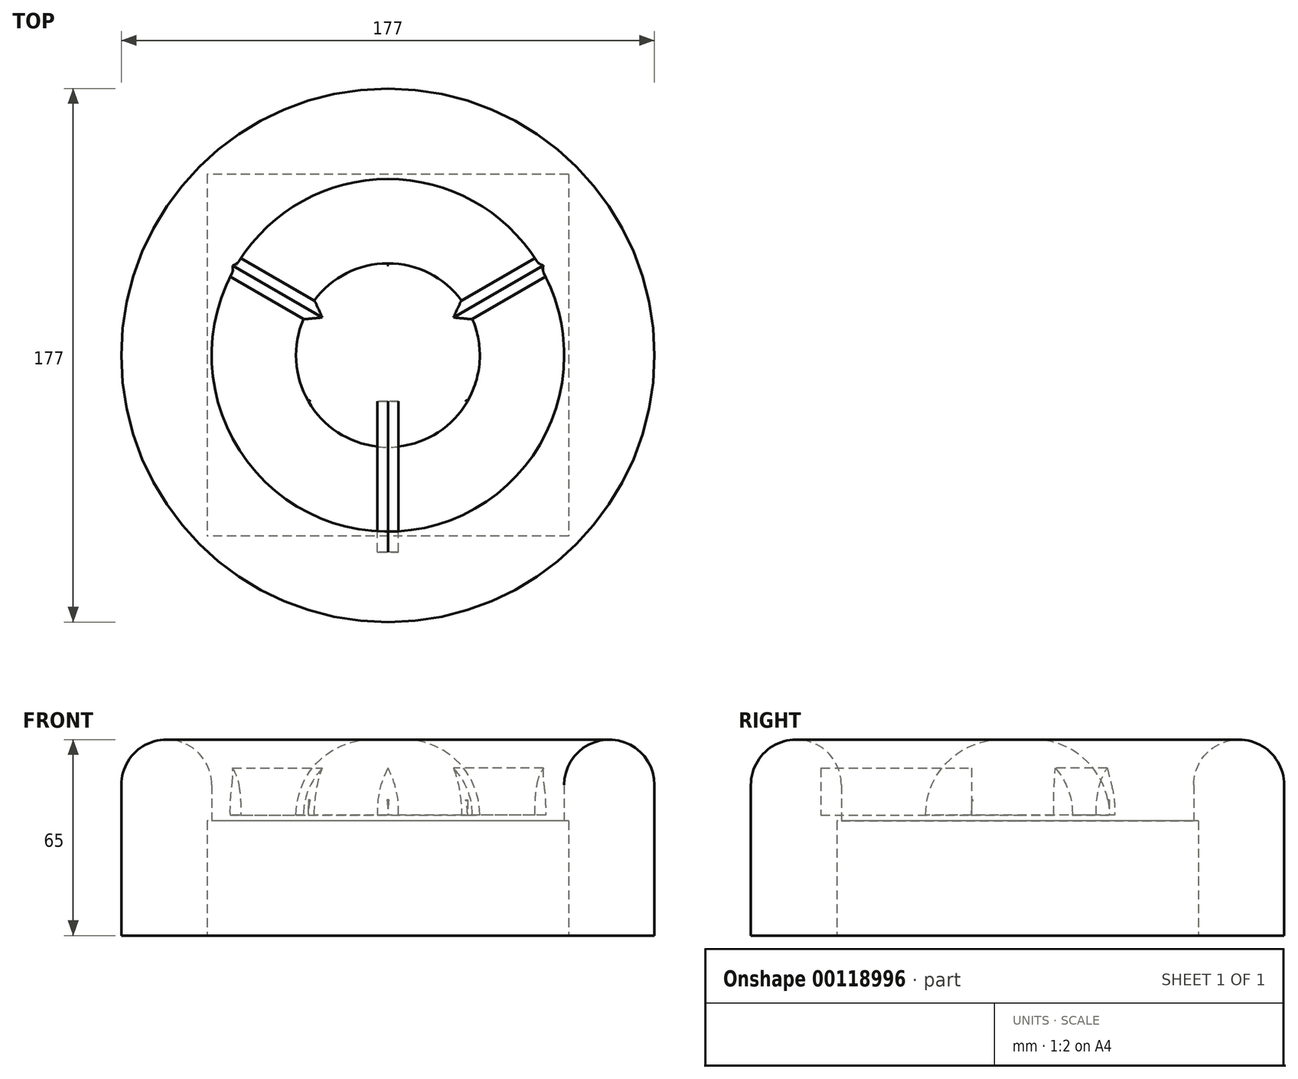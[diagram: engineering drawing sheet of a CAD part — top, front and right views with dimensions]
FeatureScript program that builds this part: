
annotation { "Feature Type Name" : "Feature", "Feature Type Description" : "" }
export const myFeature = defineFeature(function(context is Context, id is Id, definition is map)
    precondition{}
    {
        {
            var Q0;
            Q0=qCreatedBy(makeId("Top.planeOp"),FACE);
            var sketch = newSketch(context, id + "F0", { "sketchPlane" : qUnion([Q0])});
            skCircle(sketch, "E0", {"center": v(0, 0) * mm, "radius": 30.5 * mm});
            skCircle(sketch, "E1", {"center": v(0, 0) * mm, "radius": 58.5 * mm});
            skCircle(sketch, "E2", {"center": v(0, 0) * mm, "radius": 88.5 * mm});
            skLineSegment(sketch, "E3", {"start": v(0, 30.5) * mm, "end": v(-26.41, -15.25) * mm});
            skLineSegment(sketch, "E4", {"start": v(0, 30.5) * mm, "end": v(26.41, -15.25) * mm});
            skLineSegment(sketch, "E5", {"start": v(-26.41, -15.25) * mm, "end": v(26.41, -15.25) * mm});
            skSolve(sketch);
        }
        {
            var Q0;
            Q0=makeQuery(id+"F0.imprint","IMPRINT",FACE,{"disambiguationData":[TD([[makeQuery(id+"F0.imprint","IMPRINT",EDGE,{"derivedFrom":sQuery(id+"F0.wireOp",EDGE,"E0")}),1.0]])]});
            var Q1;
            Q1=makeQuery(id+"F0.imprint","IMPRINT",FACE,{"disambiguationData":[TD([[makeQuery(id+"F0.imprint","IMPRINT",EDGE,{"derivedFrom":sQuery(id+"F0.wireOp",EDGE,"E3")}),1.0]])]});
            extrude(context, id + "F1", {"entities" : qUnion([Q0, Q1]), "depth" : 25 * mm});
        }
        {
            var Q0;
            Q0=makeQuery(id+"F0.imprint","IMPRINT",FACE,{"disambiguationData":[TD([[makeQuery(id+"F0.imprint","IMPRINT",EDGE,{"derivedFrom":sQuery(id+"F0.wireOp",EDGE,"E3")}),1.0]])]});
            extrude(context, id + "F2", {"entities" : qUnion([Q0]), "depth" : 5 * mm});
        }
        {
            var Q0;
            Q0=makeQuery(id+"F1.opExtrude","CAP_EDGE",EDGE,{"disambiguationData":[OSD([sQuery(id+"F0.wireOp",EDGE,"E0")])],"isStart":false});
            fillet(context, id + "F3", {"entities" : qUnion([Q0]), "radius" : 25 * mm, "tangentPropagation" : true, "allowEdgeOverflow" : false});
        }
        {
            var Q0;
            Q0 = qSketchRegion(id + "F0", true);
            extrude(context, id + "F4", {"entities" : qUnion([Q0]), "depth" : 25 * mm, "hasSecondDirection" : true, "secondDirectionOppositeDirection" : true, "secondDirectionDepth" : 40 * mm});
        }
        {
            var Q0;
            Q0=makeQuery(id+"F4.opExtrude","CAP_FACE",FACE,{"disambiguationData":[OSD([sQuery(id+"F0.wireOp",EDGE,"E1"),sQuery(id+"F0.wireOp",EDGE,"E2")])],"isStart":false});
            var Q1;
            Q1=makeQuery(id+"F4.opExtrude","CAP_EDGE",EDGE,{"disambiguationData":[OSD([sQuery(id+"F0.wireOp",EDGE,"E2")])],"isStart":false});
            var Q2;
            Q2=makeQuery(id+"F4.opExtrude","CAP_EDGE",EDGE,{"disambiguationData":[OSD([sQuery(id+"F0.wireOp",EDGE,"E1")])],"isStart":false});
            fillet(context, id + "F5", {"entities" : qUnion([Q0, Q1, Q2]), "radius" : 15 * mm, "tangentPropagation" : true, "allowEdgeOverflow" : false});
        }
        {
            var Q0;
            Q0=makeQuery(id+"F4.opExtrude","CAP_FACE",FACE,{"disambiguationData":[OSD([sQuery(id+"F0.wireOp",EDGE,"E1"),sQuery(id+"F0.wireOp",EDGE,"E2")])],"isStart":true});
            var sketch = newSketch(context, id + "F6", { "sketchPlane" : qUnion([Q0])});
            skLineSegment(sketch, "E6.bottom", {"start": v(60, -60) * mm, "end": v(-60, -60) * mm});
            skLineSegment(sketch, "E6.top", {"start": v(60, 60) * mm, "end": v(-60, 60) * mm});
            skLineSegment(sketch, "E6.left", {"start": v(60, -60) * mm, "end": v(60, 60) * mm});
            skLineSegment(sketch, "E6.right", {"start": v(-60, -60) * mm, "end": v(-60, 60) * mm});
            skPoint(sketch, "E6.middle", {"position": v(0, 0) * mm});
            skSolve(sketch);
        }
        {
            var Q0;
            Q0=makeQuery(id+"F6.imprint","IMPRINT",FACE,{"disambiguationData":[TD([[makeQuery(id+"F6.imprint","IMPRINT",EDGE,{"derivedFrom":sQuery(id+"F6.wireOp",EDGE,"E6.bottom")}),-1.0]])]});
            extrude(context, id + "F7", {"entities" : qUnion([Q0]), "operationType" : NewBodyOperationType.REMOVE, "oppositeDirection" : true, "depth" : 38 * mm});
        }
        {
            var Q0;
            Q0=makeQuery(id+"F2.opExtrude","SWEPT_FACE",FACE,{"disambiguationData":[OSD([sQuery(id+"F0.wireOp",EDGE,"E5")])]});
            var sketch = newSketch(context, id + "F8", { "sketchPlane" : qUnion([Q0])});
            skArc(sketch, "E7", {"start": v(3.5, 0) * mm, "mid": v(2.8, 8) * mm, "end": v(0, 15.53) * mm});
            skArc(sketch, "E8", {"start": v(0, 15.53) * mm, "mid": v(-2.8, 8) * mm, "end": v(-3.5, 0) * mm});
            skLineSegment(sketch, "E9", {"start": v(-3.5, 0) * mm, "end": v(3.5, 0) * mm});
            skSolve(sketch);
        }
        {
            var Q0;
            Q0 = qSketchRegion(id + "F8", true);
            extrude(context, id + "F9", {"entities" : qUnion([Q0]), "depth" : 50 * mm});
        }
        {
            var Q0;
            Q0=makeQuery(id+"F2.opExtrude","SWEPT_FACE",FACE,{"disambiguationData":[OSD([sQuery(id+"F0.wireOp",EDGE,"E3")])]});
            var sketch = newSketch(context, id + "F10", { "sketchPlane" : qUnion([Q0])});
            skArc(sketch, "E10", {"start": v(3.5, 0) * mm, "mid": v(2.8, 8) * mm, "end": v(0, 15.53) * mm});
            skArc(sketch, "E11", {"start": v(0, 15.53) * mm, "mid": v(-2.8, 8) * mm, "end": v(-3.5, 0) * mm});
            skLineSegment(sketch, "E12", {"start": v(-3.5, 0) * mm, "end": v(3.5, 0) * mm});
            skSolve(sketch);
        }
        {
            var Q0;
            {var subQ0=sQuery(id+"F10.wireOp",EDGE,"E11");var subQ1=sQuery(id+"F10.wireOp",EDGE,"E10");var subQ2=makeQuery(id+"F10.imprint","INTERSECT",VERTEX,{"derivedFrom":[subQ1,subQ0]});Q0=makeQuery(id+"F10.imprint","IMPRINT",FACE,{"disambiguationData":[TD([[makeQuery(id+"F10.imprint","IMPRINT",EDGE,{"disambiguationData":[TD([[subQ2,1.0]])],"derivedFrom":subQ1}),1.0]])]});}
            var Q1;
            {var subQ0=sQuery(id+"F10.wireOp",EDGE,"E12");Q1=makeQuery(id+"F10.imprint","IMPRINT",FACE,{"disambiguationData":[TD([[makeQuery(id+"F10.imprint","IMPRINT",EDGE,{"derivedFrom":subQ0}),1.0]])]});}
            extrude(context, id + "F11", {"entities" : qUnion([Q0, Q1]), "operationType" : NewBodyOperationType.ADD, "depth" : 50 * mm});
        }
        {
            var Q0;
            Q0=makeQuery(id+"F2.opExtrude","SWEPT_FACE",FACE,{"disambiguationData":[OSD([sQuery(id+"F0.wireOp",EDGE,"E4")])]});
            var sketch = newSketch(context, id + "F12", { "sketchPlane" : qUnion([Q0])});
            skArc(sketch, "E13", {"start": v(3.5, 0) * mm, "mid": v(2.8, 8) * mm, "end": v(0, 15.53) * mm});
            skArc(sketch, "E14", {"start": v(0, 15.53) * mm, "mid": v(-2.8, 8) * mm, "end": v(-3.5, 0) * mm});
            skLineSegment(sketch, "E15", {"start": v(-3.5, 0) * mm, "end": v(3.5, 0) * mm});
            skSolve(sketch);
        }
        {
            var Q0;
            {var subQ0=sQuery(id+"F12.wireOp",EDGE,"E15");Q0=makeQuery(id+"F12.imprint","IMPRINT",FACE,{"disambiguationData":[TD([[makeQuery(id+"F12.imprint","IMPRINT",EDGE,{"derivedFrom":subQ0}),-1.0]])]});}
            var Q1;
            {var subQ0=sQuery(id+"F12.wireOp",EDGE,"E14");var subQ1=sQuery(id+"F12.wireOp",EDGE,"E13");var subQ2=makeQuery(id+"F12.imprint","INTERSECT",VERTEX,{"derivedFrom":[subQ1,subQ0]});Q1=makeQuery(id+"F12.imprint","IMPRINT",FACE,{"disambiguationData":[TD([[makeQuery(id+"F12.imprint","IMPRINT",EDGE,{"disambiguationData":[TD([[subQ2,1.0]])],"derivedFrom":subQ1}),1.0]])]});}
            extrude(context, id + "F13", {"entities" : qUnion([Q0, Q1]), "operationType" : NewBodyOperationType.ADD, "depth" : 50 * mm});
        }
    });
